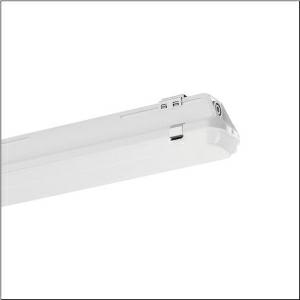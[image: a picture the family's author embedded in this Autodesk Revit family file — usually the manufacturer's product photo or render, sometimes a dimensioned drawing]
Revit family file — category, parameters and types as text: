
# Revit family: monsun_r__21_51fb207p480b_726c
name_source: partatom
category: Lighting Fixtures
units: mm (PartAtom-declared; Revit-internal decimal feet)

## family parameters
Cut with Voids When Loaded = No
Host = Face
Light Source = No
Part Type = Normal
Room Calculation Point = No
Round Connector Dimension = Use Diameter
Shared = No

## types (1)
- Monsun® 21 (1 x LED, 7270 lm, 52.8 W, 4000K)
    Apparent Load = 53 VA
    CIE Flux Codes = 45 75 93 94 100
    Color Rendering = 80
    Color Temperature = 4000K
    Default Elevation = 1800 mm
    Description = Monsun® 21, damp-proof luminaire, chain hanger, primary optical cover: enclosure, of PC, light emission: direct distribution, primary light characteristic: symmetric, installation type: suspended mounting, surface-mounted, horizontal mounting, vertical mounting, LED, rated luminous flux: 7.270lm, luminous efficacy: 138lm/W, light colour: 840, colour temperature: 4000K, control gear: ECG, with terminal, 3-pole, max. 2.5mm², mains connection: 220..240V, AC, 50/60Hz, rated input power: 53W, housing, of glass-fibre reinforced polyester, uncoated, bright grey, length: 1.590mm, width: 90mm, height: 88mm, clip for enclosure, of stainless steel (V2A), ceiling mounting element, of stainless steel (V2A), chain hanger, of stainless steel (V2A), protection rating (complete): IP66, insulation class (complete): insulation class I (protective earthing), certification: CE, ENEC, VDE, UKCA, protection symbol: D, impact resistance: IK08, permissible operating ambient temperature: -25..+35°C, standard: EN 50419, EN 60598-2-1, corresponds to IFS (International Featured Standards) requirements for safety and quality in the food industry, for indoor or canopied outdoor use, no direct snow, no direct sun, no direct rain, packaging unit: 1 piece
    Height = 89 mm
    Lamp = 1 x LED
    Lamp Light Flux = 7270 lm
    Lamp Power = 52.8 W
    Lamp count = 1
    Length = 1590 mm
    Luminous efficacy = 138 lm/W
    Manufacturer = Siteco
    ModVariant = No
    Model = 51FB207P480B
    Mounting Place = Ceiling
    Mounting Type = Pendant
    Number of Poles = 1
    OnlyDefault = Yes
    Power Factor = 1
    Product Name = Monsun® 21
    Product group = damp-proof luminaire | ceiling pendant
    ProductGroupID = 908
    Protection Class = Protection class I
    Protection Degree = IP 66
    RLX_Detail_Level = 1
    RlxData = <blob elided: 88257 chars, md5=90a730f7>
    Socket = socket
    Standby Power = 0 W
    System Light Flux = 7270 lm
    System Power = 53 W
    Type Comments = Product without accessories
    Type Image = l_1006717.jpg
    URL = http://relux.com
    VarID = ---
    Voltage = 0 V
    Weight = 0.00 kg
    Width = 90 mm

## geometry (parser evidence)
native form markers: Blend x4, Sweep x15
no freeform markers — native parametric forms only
